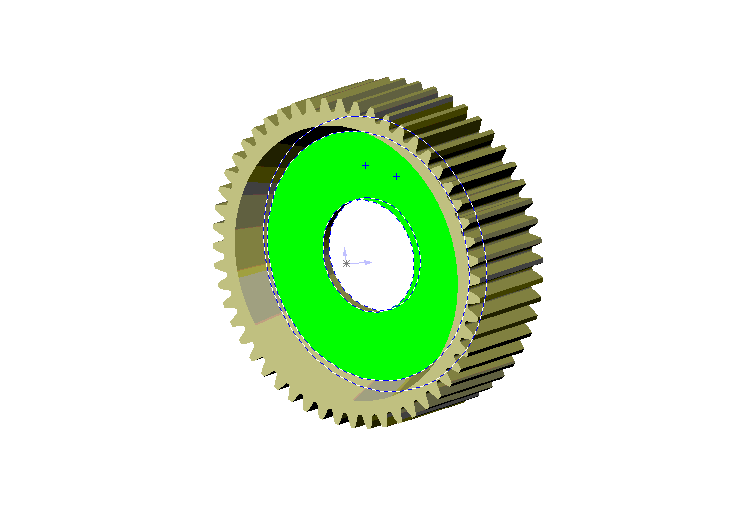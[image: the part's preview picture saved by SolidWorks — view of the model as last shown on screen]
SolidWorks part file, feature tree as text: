
SOLIDWORKS PART (.sldprt)
format: sldprt  version: not decoded by parser v0  size: 526,336 bytes
history: native  units: mm
features: sketch x19, plane x4, cut_extrude x3, material x1, fillet x1, pattern_circular x1 (+8 scaffold rows collapsed)
feature tree (37):
  scaffold x8  (default folders/planes/origin — collapsed)
  material  "Matériau <non spécifié>"
  plane  "Plane1"
  plane  "Plane2"
  plane  "Plane3"
  sketch  "Esquisse1"  dims[c1.D2=15.6mm c1.D1=42.0mm c2.D1=~3.461538deg]
  sketch  "Esquisse2"  dims[c1.D2=~15.286402mm c1.D1=37.0mm c2.D1=~4.231213deg]
  sketch  "Esquisse3"  dims[c1.D2=~14.972803mm c1.D1=33.0mm c2.D1=~4.83462deg]
  sketch  "Esquisse4"  dims[c1.D2=~14.659205mm c1.D1=30.0mm c2.D1=~5.169455deg]
  sketch  "Esquisse5"  dims[c1.D2=15.8mm c1.D1=46.0mm c2.D1=~2.902033deg]
  sketch  "Esquisse6"  dims[c1.D2=16.0mm c1.D1=50.0mm c2.D1=~2.296754deg]
  sketch  "Esquisse7"  dims[c1.D2=16.2mm c1.D1=54.0mm c2.D1=~1.650463deg]
  plane  "Plan1"  Offset=10mm
  sketch  "Esquisse8"  dims[c1.D2=15.6mm c1.D1=18.0mm c2.D1=~3.461538deg]
  sketch  "Esquisse9"  dims[c1.D2=~15.286402mm c1.D1=15.0mm c2.D1=~4.231213deg]
  sketch  "Esquisse10"  dims[c1.D2=~14.972803mm c1.D1=13.0mm c2.D1=~4.83462deg]
  sketch  "Esquisse11"  dims[c1.D2=~14.659205mm c1.D1=12.0mm c2.D1=~5.169455deg]
  sketch  "Esquisse12"  dims[c1.D2=15.8mm c1.D1=20.0mm c2.D1=~2.902033deg]
  sketch  "Esquisse13"  dims[c1.D2=16.0mm c1.D1=21.0mm c2.D1=~2.296754deg]
  sketch  "Esquisse14"  dims[c1.D2=16.2mm c1.D1=22.0mm c2.D1=~1.650463deg]
  sketch  "Esquisse15"  dims[D1=29.7mm]
  sketch  "Esquisse16"  dims[D1=29.7mm]
  fillet  "Congé1"  Radius=0.25mm
  pattern_circular  "Répétition circulaire1"  Count=52 Angle=360deg
  sketch  "Esquisse17"  dims[D1=27.0mm]
  cut_extrude  "Enlèv. mat.-Extru.1"  Depth=3.5mm
  sketch  "Esquisse18"  dims[D1=27.0mm]
  cut_extrude  "Enlèv. mat.-Extru.2"  Depth=5.5mm
  sketch  "Esquisse19"  dims[D1=11.0mm]
  cut_extrude  "Enlèv. mat.-Extru.3"  [1 undecoded]
decode coverage: 23 of 24 modeling features carry decoded parameters
note: ~ marks probable driven/reference dimensions
note: 1 parameter value undecoded
note: suppression state not decoded; provenance and decode notes live in map.json
